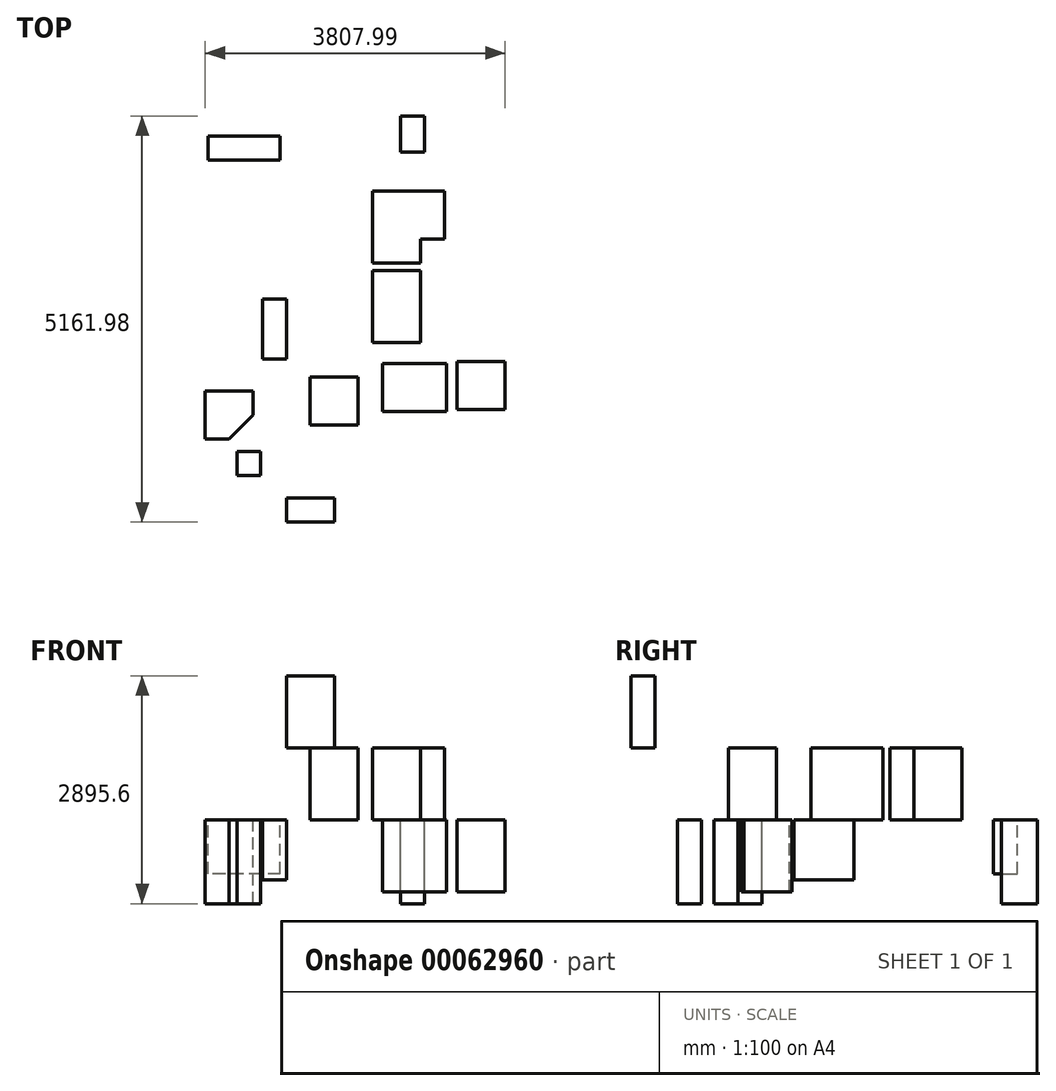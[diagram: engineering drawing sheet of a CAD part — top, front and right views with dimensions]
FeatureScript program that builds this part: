
annotation { "Feature Type Name" : "Feature", "Feature Type Description" : "" }
export const myFeature = defineFeature(function(context is Context, id is Id, definition is map)
    precondition{}
    {
        {
            var Q0;
            Q0=qCreatedBy(makeId("Top.planeOp"),FACE);
            var sketch = newSketch(context, id + "F0", { "sketchPlane" : qUnion([Q0])});
            skLineSegment(sketch, "E0.bottom", {"start": v(-355.43, -411) * mm, "end": v(254.17, -411) * mm});
            skLineSegment(sketch, "E0.top", {"start": v(-355.43, 503.4) * mm, "end": v(254.17, 503.4) * mm});
            skLineSegment(sketch, "E0.left", {"start": v(-355.43, -411) * mm, "end": v(-355.43, 503.4) * mm});
            skLineSegment(sketch, "E0.right", {"start": v(254.17, -411) * mm, "end": v(254.17, 503.4) * mm});
            skSolve(sketch);
        }
        {
            var Q0;
            Q0 = qSketchRegion(id + "F0", true);
            var Q1;
            Q1 = qSketchRegion(id + "F2", true);
            extrude(context, id + "F1", {"entities" : qUnion([Q0, Q1]), "depth" : 914.4 * mm});
        }
        {
            var Q0;
            Q0=makeQuery(id+"F1.opExtrude","CAP_FACE",FACE,{"disambiguationData":[OSD([sQuery(id+"F0.wireOp",EDGE,"E0.bottom"),sQuery(id+"F0.wireOp",EDGE,"E0.top"),sQuery(id+"F0.wireOp",EDGE,"E0.left"),sQuery(id+"F0.wireOp",EDGE,"E0.right")])],"isStart":true});
            var sketch = newSketch(context, id + "F2", { "sketchPlane" : qUnion([Q0])});
            skLineSegment(sketch, "E1", {"start": v(254.17, -595.41) * mm, "end": v(254.17, -900.21) * mm});
            skLineSegment(sketch, "E2", {"start": v(254.17, -900.21) * mm, "end": v(558.97, -900.21) * mm});
            skLineSegment(sketch, "E3", {"start": v(558.97, -900.21) * mm, "end": v(558.97, -1509.81) * mm});
            skLineSegment(sketch, "E4", {"start": v(558.97, -1509.81) * mm, "end": v(-355.43, -1509.81) * mm});
            skLineSegment(sketch, "E5", {"start": v(-355.43, -1509.81) * mm, "end": v(-355.43, -595.41) * mm});
            skLineSegment(sketch, "E6", {"start": v(-355.43, -595.41) * mm, "end": v(254.17, -595.41) * mm});
            skSolve(sketch);
        }
        {
            var Q0;
            Q0 = qSketchRegion(id + "F2", true);
            extrude(context, id + "F3", {"entities" : qUnion([Q0]), "oppositeDirection" : true, "depth" : 914.4 * mm});
        }
        {
            var Q0;
            Q0=makeQuery(id+"F1.opExtrude","CAP_FACE",FACE,{"disambiguationData":[OSD([sQuery(id+"F0.wireOp",EDGE,"E0.bottom"),sQuery(id+"F0.wireOp",EDGE,"E0.top"),sQuery(id+"F0.wireOp",EDGE,"E0.left"),sQuery(id+"F0.wireOp",EDGE,"E0.right")])],"isStart":true});
            var sketch = newSketch(context, id + "F4", { "sketchPlane" : qUnion([Q0])});
            skLineSegment(sketch, "E7.bottom", {"start": v(715.78, 1263.05) * mm, "end": v(1325.38, 1263.05) * mm});
            skLineSegment(sketch, "E7.top", {"start": v(715.78, 653.45) * mm, "end": v(1325.38, 653.45) * mm});
            skLineSegment(sketch, "E7.left", {"start": v(715.78, 1263.05) * mm, "end": v(715.78, 653.45) * mm});
            skLineSegment(sketch, "E7.right", {"start": v(1325.38, 1263.05) * mm, "end": v(1325.38, 653.45) * mm});
            skSolve(sketch);
        }
        {
            var Q0;
            Q0 = qSketchRegion(id + "F4", true);
            extrude(context, id + "F5", {"entities" : qUnion([Q0]), "depth" : 914.4 * mm});
        }
        {
            var Q0;
            Q0=makeQuery(id+"F1.opExtrude","CAP_FACE",FACE,{"disambiguationData":[OSD([sQuery(id+"F0.wireOp",EDGE,"E0.bottom"),sQuery(id+"F0.wireOp",EDGE,"E0.top"),sQuery(id+"F0.wireOp",EDGE,"E0.left"),sQuery(id+"F0.wireOp",EDGE,"E0.right")])],"isStart":true});
            var sketch = newSketch(context, id + "F6", { "sketchPlane" : qUnion([Q0])});
            skLineSegment(sketch, "E8.bottom", {"start": v(584.17, 1291.1) * mm, "end": v(-228.63, 1291.1) * mm});
            skLineSegment(sketch, "E8.top", {"start": v(584.17, 681.5) * mm, "end": v(-228.63, 681.5) * mm});
            skLineSegment(sketch, "E8.left", {"start": v(584.17, 1291.1) * mm, "end": v(584.17, 681.5) * mm});
            skLineSegment(sketch, "E8.right", {"start": v(-228.63, 1291.1) * mm, "end": v(-228.63, 681.5) * mm});
            skSolve(sketch);
        }
        {
            var Q0;
            Q0 = qSketchRegion(id + "F6", true);
            extrude(context, id + "F7", {"entities" : qUnion([Q0]), "depth" : 914.4 * mm});
        }
        {
            var Q0;
            Q0=makeQuery(id+"F7.opExtrude","CAP_FACE",FACE,{"disambiguationData":[OSD([sQuery(id+"F6.wireOp",EDGE,"E8.bottom"),sQuery(id+"F6.wireOp",EDGE,"E8.top"),sQuery(id+"F6.wireOp",EDGE,"E8.left"),sQuery(id+"F6.wireOp",EDGE,"E8.right")])],"isStart":true});
            var sketch = newSketch(context, id + "F8", { "sketchPlane" : qUnion([Q0])});
            skLineSegment(sketch, "E9.bottom", {"start": v(-542.88, -1460.41) * mm, "end": v(-1152.48, -1460.41) * mm});
            skLineSegment(sketch, "E9.top", {"start": v(-542.88, -850.81) * mm, "end": v(-1152.48, -850.81) * mm});
            skLineSegment(sketch, "E9.left", {"start": v(-542.88, -1460.41) * mm, "end": v(-542.88, -850.81) * mm});
            skLineSegment(sketch, "E9.right", {"start": v(-1152.48, -1460.41) * mm, "end": v(-1152.48, -850.81) * mm});
            skSolve(sketch);
        }
        {
            var Q0;
            Q0 = qSketchRegion(id + "F8", true);
            extrude(context, id + "F9", {"entities" : qUnion([Q0]), "depth" : 914.4 * mm});
        }
        {
            var Q0;
            Q0=makeQuery(id+"F9.opExtrude","CAP_FACE",FACE,{"disambiguationData":[OSD([sQuery(id+"F8.wireOp",EDGE,"E9.bottom"),sQuery(id+"F8.wireOp",EDGE,"E9.top"),sQuery(id+"F8.wireOp",EDGE,"E9.left"),sQuery(id+"F8.wireOp",EDGE,"E9.right")])],"isStart":false});
            var sketch = newSketch(context, id + "F10", { "sketchPlane" : qUnion([Q0])});
            skLineSegment(sketch, "E10.bottom", {"start": v(-840.93, -2391.2) * mm, "end": v(-1450.53, -2391.2) * mm});
            skLineSegment(sketch, "E10.top", {"start": v(-840.93, -2696) * mm, "end": v(-1450.53, -2696) * mm});
            skLineSegment(sketch, "E10.left", {"start": v(-840.93, -2391.2) * mm, "end": v(-840.93, -2696) * mm});
            skLineSegment(sketch, "E10.right", {"start": v(-1450.53, -2391.2) * mm, "end": v(-1450.53, -2696) * mm});
            skLineSegment(sketch, "E11.left", {"start": v(-1450.53, -2391.2) * mm, "end": v(-1450.53, -2696.88) * mm});
            skSolve(sketch);
        }
        {
            var Q0;
            Q0 = qSketchRegion(id + "F10", true);
            extrude(context, id + "F11", {"entities" : qUnion([Q0]), "depth" : 914.4 * mm});
        }
        {
            var Q0;
            Q0=makeQuery(id+"F9.opExtrude","CAP_FACE",FACE,{"disambiguationData":[OSD([sQuery(id+"F8.wireOp",EDGE,"E9.bottom"),sQuery(id+"F8.wireOp",EDGE,"E9.top"),sQuery(id+"F8.wireOp",EDGE,"E9.left"),sQuery(id+"F8.wireOp",EDGE,"E9.right")])],"isStart":true});
            var sketch = newSketch(context, id + "F12", { "sketchPlane" : qUnion([Q0])});
            skLineSegment(sketch, "E12", {"start": v(-1873.01, 1029.88) * mm, "end": v(-1873.01, 1334.68) * mm});
            skLineSegment(sketch, "E13", {"start": v(-1873.01, 1334.68) * mm, "end": v(-2177.81, 1640.54) * mm});
            skLineSegment(sketch, "E14", {"start": v(-1873.01, 1029.88) * mm, "end": v(-2482.61, 1029.88) * mm});
            skLineSegment(sketch, "E15", {"start": v(-2482.61, 1029.88) * mm, "end": v(-2482.61, 1640.54) * mm});
            skLineSegment(sketch, "E16", {"start": v(-2482.61, 1640.54) * mm, "end": v(-2177.81, 1640.54) * mm});
            skSolve(sketch);
        }
        {
            var Q0;
            Q0 = qSketchRegion(id + "F12", true);
            extrude(context, id + "F13", {"entities" : qUnion([Q0]), "depth" : 1066.8 * mm});
        }
        {
            var Q0;
            Q0=makeQuery(id+"F9.opExtrude","CAP_FACE",FACE,{"disambiguationData":[OSD([sQuery(id+"F8.wireOp",EDGE,"E9.bottom"),sQuery(id+"F8.wireOp",EDGE,"E9.top"),sQuery(id+"F8.wireOp",EDGE,"E9.left"),sQuery(id+"F8.wireOp",EDGE,"E9.right")])],"isStart":true});
            var sketch = newSketch(context, id + "F14", { "sketchPlane" : qUnion([Q0])});
            skLineSegment(sketch, "E17.bottom", {"start": v(-1777.05, 1800.87) * mm, "end": v(-2081.85, 1800.87) * mm});
            skLineSegment(sketch, "E17.top", {"start": v(-1777.05, 2105.67) * mm, "end": v(-2081.85, 2105.67) * mm});
            skLineSegment(sketch, "E17.left", {"start": v(-1777.05, 1800.87) * mm, "end": v(-1777.05, 2105.67) * mm});
            skLineSegment(sketch, "E17.right", {"start": v(-2081.85, 1800.87) * mm, "end": v(-2081.85, 2105.67) * mm});
            skSolve(sketch);
        }
        {
            var Q0;
            Q0 = qSketchRegion(id + "F14", true);
            extrude(context, id + "F15", {"entities" : qUnion([Q0]), "depth" : 1066.8 * mm});
        }
        {
            var Q0;
            Q0=makeQuery(id+"F9.opExtrude","CAP_FACE",FACE,{"disambiguationData":[OSD([sQuery(id+"F8.wireOp",EDGE,"E9.bottom"),sQuery(id+"F8.wireOp",EDGE,"E9.top"),sQuery(id+"F8.wireOp",EDGE,"E9.left"),sQuery(id+"F8.wireOp",EDGE,"E9.right")])],"isStart":true});
            var sketch = newSketch(context, id + "F16", { "sketchPlane" : qUnion([Q0])});
            skLineSegment(sketch, "E18.bottom", {"start": v(-1451.14, -137.9) * mm, "end": v(-1755.94, -137.9) * mm});
            skLineSegment(sketch, "E18.top", {"start": v(-1451.14, 624.1) * mm, "end": v(-1755.94, 624.1) * mm});
            skLineSegment(sketch, "E18.left", {"start": v(-1451.14, -137.9) * mm, "end": v(-1451.14, 624.1) * mm});
            skLineSegment(sketch, "E18.right", {"start": v(-1755.94, -137.9) * mm, "end": v(-1755.94, 624.1) * mm});
            skSolve(sketch);
        }
        {
            var Q0;
            Q0 = qSketchRegion(id + "F16", true);
            extrude(context, id + "F17", {"entities" : qUnion([Q0]), "depth" : 762 * mm});
        }
        {
            var Q0;
            Q0=makeQuery(id+"F3.opExtrude","CAP_FACE",FACE,{"disambiguationData":[OSD([sQuery(id+"F2.wireOp",EDGE,"E1"),sQuery(id+"F2.wireOp",EDGE,"E2"),sQuery(id+"F2.wireOp",EDGE,"E3"),sQuery(id+"F2.wireOp",EDGE,"E4"),sQuery(id+"F2.wireOp",EDGE,"E5"),sQuery(id+"F2.wireOp",EDGE,"E6")])],"isStart":true});
            var sketch = newSketch(context, id + "F18", { "sketchPlane" : qUnion([Q0])});
            skLineSegment(sketch, "E19.bottom", {"start": v(-1533.43, -1904.9) * mm, "end": v(-2447.83, -1904.9) * mm});
            skLineSegment(sketch, "E19.top", {"start": v(-1533.43, -2209.7) * mm, "end": v(-2447.83, -2209.7) * mm});
            skLineSegment(sketch, "E19.left", {"start": v(-1533.43, -1904.9) * mm, "end": v(-1533.43, -2209.7) * mm});
            skLineSegment(sketch, "E19.right", {"start": v(-2447.83, -1904.9) * mm, "end": v(-2447.83, -2209.7) * mm});
            skSolve(sketch);
        }
        {
            var Q0;
            Q0 = qSketchRegion(id + "F18", true);
            extrude(context, id + "F19", {"entities" : qUnion([Q0]), "depth" : 685.8 * mm});
        }
        {
            var Q0;
            Q0=makeQuery(id+"F3.opExtrude","CAP_FACE",FACE,{"disambiguationData":[OSD([sQuery(id+"F2.wireOp",EDGE,"E1"),sQuery(id+"F2.wireOp",EDGE,"E2"),sQuery(id+"F2.wireOp",EDGE,"E3"),sQuery(id+"F2.wireOp",EDGE,"E4"),sQuery(id+"F2.wireOp",EDGE,"E5"),sQuery(id+"F2.wireOp",EDGE,"E6")])],"isStart":true});
            var sketch = newSketch(context, id + "F20", { "sketchPlane" : qUnion([Q0])});
            skLineSegment(sketch, "E20.bottom", {"start": v(304.8, -2008.78) * mm, "end": v(0, -2008.78) * mm});
            skLineSegment(sketch, "E20.top", {"start": v(304.8, -2465.98) * mm, "end": v(0, -2465.98) * mm});
            skLineSegment(sketch, "E20.left", {"start": v(304.8, -2008.78) * mm, "end": v(304.8, -2465.98) * mm});
            skLineSegment(sketch, "E20.right", {"start": v(0, -2008.78) * mm, "end": v(0, -2465.98) * mm});
            skSolve(sketch);
        }
        {
            var Q0;
            Q0 = qSketchRegion(id + "F20", true);
            extrude(context, id + "F21", {"entities" : qUnion([Q0]), "depth" : 1066.8 * mm});
        }
    });
